FREECAD ASSEMBLY — COMPONENT RECIPES ("composit_stand3_base_part_assembly")

This assembly document has 2 components, labeled P0..P1 below (a component is one placed body or linked part). 0 of them carry a construction recipe — the FreeCAD feature program that regenerates the part from scratch, quoted from this document or its linked companion documents; the rest are supplied as boundary geometry only. No exploded tour is included for this assembly.
COMPONENT P0 — geometry summary ("Assembly"; no construction recipe available for this part):
  bounding box: 1447.7 x 623.7 x 581.1 mm
  tessellated surface: 18,192 triangles
  volume: 19231758281030380541861970115208508867489059734913730402973165908609705601683032416294708616993295040512 mm^3 (3665335281025753463477664139359433207239590324829889949547303601196224774161047298806099543588864% of its bounding box)
COMPONENT P1 — geometry summary ("modules"; no construction recipe available for this part):
  bounding box: 970.0 x 621.6 x 538.5 mm
  tessellated surface: 540,144 triangles
  volume: 24614997257459501262434143274700846294563748780975734684296354434184215733008122623218899292439195942912 mm^3 (7581090288919345765553194715147032234758176838500958952249466268782488530384992003739784161787904% of its bounding box)
  symmetry: mirror-symmetric across its y mid-plane
PROVENANCE & LICENSES
A FreeCAD (.FCStd) document from a public repository crawl; recipes are the document's own serialized feature recipes (and, for linked parts, companion documents' recipes).
License: as declared in the source repository (recorded in the dataset sidecar).
